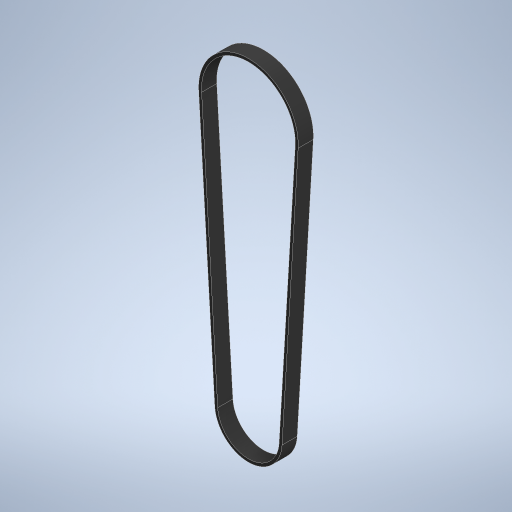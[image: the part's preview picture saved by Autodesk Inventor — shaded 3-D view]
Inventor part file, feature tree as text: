
AUTODESK INVENTOR PART (.ipt)
format: ipt  version: 2024 (Build 280153000, 153)  size: 258,048 bytes
history: native  units: in
note: dims shown in document units (in); Inventor stores cm internally (conversion verified against a paired STEP export)
features: extrude x1, sketch x1
ambient origin geometry x8: Origin, YZ Plane, XZ Plane, XY Plane, X Axis, Y Axis, Z Axis, Center Point
bodies: Solid1 (feature_tree)
feature tree (2):
  extrude  "Extrusion1"  Depth=0.3543in
  sketch  "Sketch1"  dims[d0=6.209in d1=1.504in d2=2.256in d3=0.0343in d4=0.0343in d5=0.3543in d6=0.0in]
